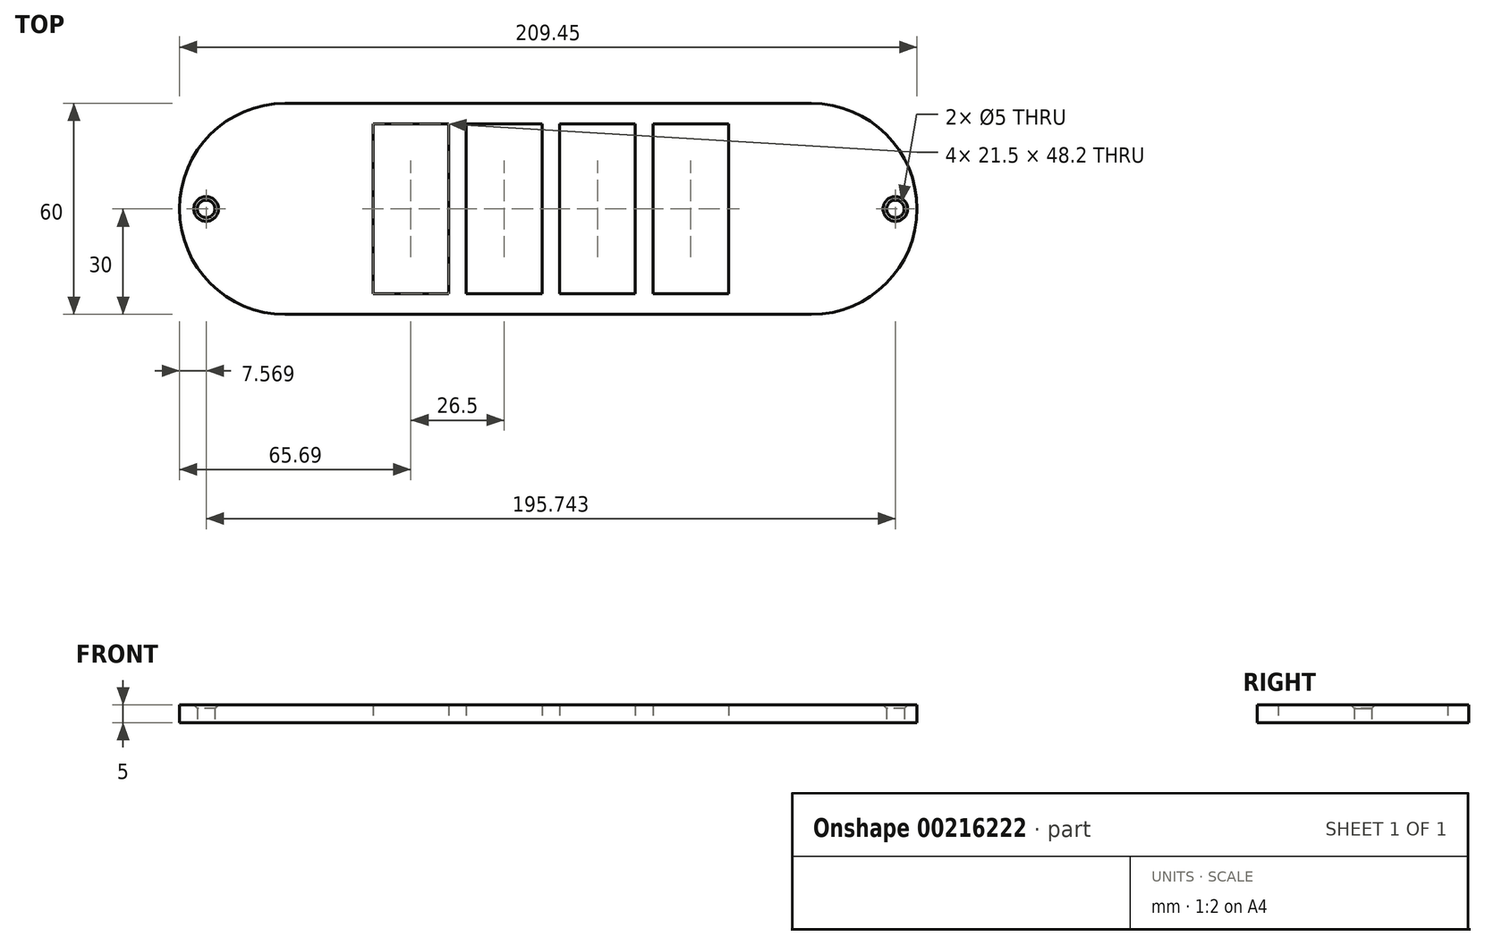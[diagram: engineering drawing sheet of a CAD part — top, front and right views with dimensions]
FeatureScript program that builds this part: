
annotation { "Feature Type Name" : "Feature", "Feature Type Description" : "" }
export const myFeature = defineFeature(function(context is Context, id is Id, definition is map)
    precondition{}
    {
        {
            var Q0;
            Q0=qCreatedBy(makeId("Top.planeOp"),FACE);
            var sketch = newSketch(context, id + "F0", { "sketchPlane" : qUnion([Q0])});
            skLineSegment(sketch, "E0.bottom", {"start": v(-75.44, 30) * mm, "end": v(74, 30) * mm});
            skLineSegment(sketch, "E0.top", {"start": v(-75.44, -30) * mm, "end": v(74, -30) * mm});
            skPoint(sketch, "E0.middle", {"position": v(0, 0) * mm});
            skArc(sketch, "E1", {"start": v(74, -30) * mm, "mid": v(104, 0) * mm, "end": v(74, 30) * mm});
            skArc(sketch, "E2", {"start": v(-75.44, 30) * mm, "mid": v(-105.44, 0) * mm, "end": v(-75.44, -30) * mm});
            skLineSegment(sketch, "E3.bottom", {"start": v(-2.5, -24.1) * mm, "end": v(-24, -24.1) * mm});
            skLineSegment(sketch, "E3.top", {"start": v(-2.5, 24.1) * mm, "end": v(-24, 24.1) * mm});
            skLineSegment(sketch, "E3.left", {"start": v(-2.5, -24.1) * mm, "end": v(-2.5, 24.1) * mm});
            skLineSegment(sketch, "E3.right", {"start": v(-24, -24.1) * mm, "end": v(-24, 24.1) * mm});
            skPoint(sketch, "E3.middle", {"position": v(-13.25, 0) * mm});
            skLineSegment(sketch, "E4.bottom", {"start": v(-29, -24.1) * mm, "end": v(-50.5, -24.1) * mm});
            skLineSegment(sketch, "E4.top", {"start": v(-29, 24.1) * mm, "end": v(-50.5, 24.1) * mm});
            skLineSegment(sketch, "E4.left", {"start": v(-29, -24.1) * mm, "end": v(-29, 24.1) * mm});
            skLineSegment(sketch, "E4.right", {"start": v(-50.5, -24.1) * mm, "end": v(-50.5, 24.1) * mm});
            skPoint(sketch, "E5.orphan", {"position": v(-100, 30) * mm});
            skPoint(sketch, "E6.orphan", {"position": v(-100, -30) * mm});
            skPoint(sketch, "E7.orphan", {"position": v(100, 30) * mm});
            skPoint(sketch, "E8.orphan", {"position": v(100, -30) * mm});
            skPoint(sketch, "E9.MirrorP", {"position": v(45.44, 0) * mm});
            skPoint(sketch, "E10.MirrorCS.end.orphan", {"position": v(50.5, 24.1) * mm});
            skPoint(sketch, "E10.MirrorCS.start.orphan", {"position": v(50.5, -24.1) * mm});
            skPoint(sketch, "E11.MirrorP", {"position": v(13.25, 0) * mm});
            skLineSegment(sketch, "E12.MirrorCS", {"start": v(29, 24.1) * mm, "end": v(50.5, 24.1) * mm});
            skLineSegment(sketch, "E13.MirrorCS", {"start": v(50.5, -24.1) * mm, "end": v(50.5, 24.1) * mm});
            skLineSegment(sketch, "E14.MirrorCS", {"start": v(29, -24.1) * mm, "end": v(50.5, -24.1) * mm});
            skLineSegment(sketch, "E15.MirrorCS", {"start": v(29, -24.1) * mm, "end": v(29, 24.1) * mm});
            skLineSegment(sketch, "E16.MirrorCS", {"start": v(24, -24.1) * mm, "end": v(24, 24.1) * mm});
            skLineSegment(sketch, "E17.MirrorCS", {"start": v(2.5, 24.1) * mm, "end": v(24, 24.1) * mm});
            skLineSegment(sketch, "E18.MirrorCS", {"start": v(2.5, -24.1) * mm, "end": v(2.5, 24.1) * mm});
            skLineSegment(sketch, "E19.MirrorCS", {"start": v(2.5, -24.1) * mm, "end": v(24, -24.1) * mm});
            skCircle(sketch, "E20", {"center": v(-97.87, 0) * mm, "radius": 2.5 * mm});
            skPoint(sketch, "E20.centerSnap0", {"position": v(-105.44, 0) * mm});
            skCircle(sketch, "E21.MirrorC", {"center": v(97.87, 0) * mm, "radius": 2.5 * mm});
            skPoint(sketch, "E22.middle", {"position": v(-82.53, 0.8) * mm});
            skPoint(sketch, "E23.MirrorP", {"position": v(-67, 0.8) * mm});
            skSolve(sketch);
        }
        {
            var Q0;
            Q0=makeQuery(id+"F0.imprint","IMPRINT",FACE,{"disambiguationData":[TD([[makeQuery(id+"F0.imprint","IMPRINT",EDGE,{"derivedFrom":sQuery(id+"F0.wireOp",EDGE,"E0.bottom")}),-1.0]])]});
            extrude(context, id + "F1", {"entities" : qUnion([Q0]), "depth" : 5 * mm});
        }
        {
            var Q0;
            Q0=makeQuery(id+"F1.opExtrude","CAP_EDGE",EDGE,{"disambiguationData":[OSD([sQuery(id+"F0.wireOp",EDGE,"E20")])],"isStart":false});
            chamfer(context, id + "F2", {"entities" : qUnion([Q0]), "width" : 1 * mm, "tangentPropagation" : true});
        }
        {
            var Q0;
            Q0=makeQuery(id+"F1.opExtrude","CAP_EDGE",EDGE,{"disambiguationData":[OSD([sQuery(id+"F0.wireOp",EDGE,"E21.MirrorC")])],"isStart":false});
            chamfer(context, id + "F3", {"entities" : qUnion([Q0]), "width" : 1 * mm, "tangentPropagation" : true});
        }
    });
